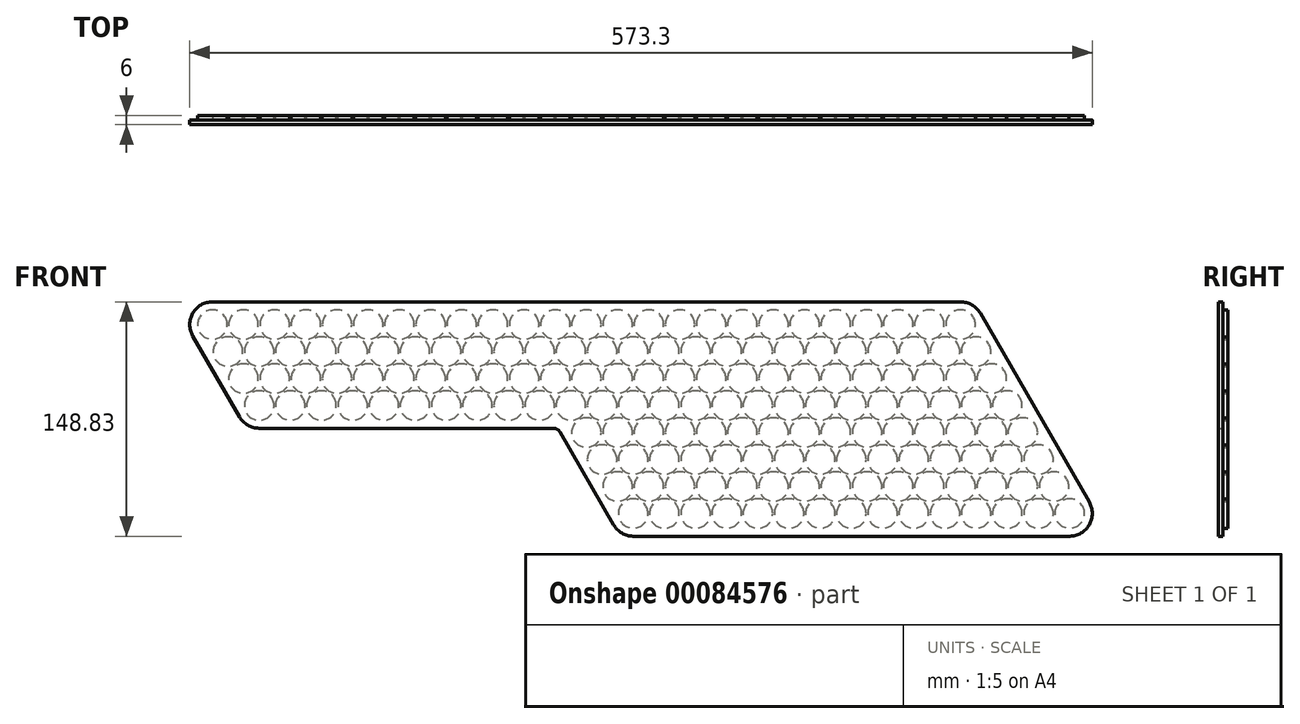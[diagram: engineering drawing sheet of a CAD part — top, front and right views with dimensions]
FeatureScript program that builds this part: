
annotation { "Feature Type Name" : "Feature", "Feature Type Description" : "" }
export const myFeature = defineFeature(function(context is Context, id is Id, definition is map)
    precondition{}
    {
        {
            var Q0;
            Q0=qCreatedBy(makeId("Front.planeOp"),FACE);
            var sketch = newSketch(context, id + "F0", { "sketchPlane" : qUnion([Q0]) });
            skCircle(sketch, "E0", {"center": v(0, 0) * mm, "radius": 9.4 * mm});
            skCircle(sketch, "E1.0.1.0", {"center": v(9.9, -17.15) * mm, "radius": 9.4 * mm});
            skCircle(sketch, "E1.0.2.0", {"center": v(19.8, -34.3) * mm, "radius": 9.4 * mm});
            skCircle(sketch, "E1.0.3.0", {"center": v(29.7, -51.44) * mm, "radius": 9.4 * mm});
            skCircle(sketch, "E1.1.0.0", {"center": v(19.8, 0) * mm, "radius": 9.4 * mm});
            skCircle(sketch, "E1.1.1.0", {"center": v(29.7, -17.15) * mm, "radius": 9.4 * mm});
            skCircle(sketch, "E1.1.2.0", {"center": v(39.6, -34.3) * mm, "radius": 9.4 * mm});
            skCircle(sketch, "E1.1.3.0", {"center": v(49.5, -51.44) * mm, "radius": 9.4 * mm});
            skCircle(sketch, "E1.2.0.0", {"center": v(39.6, 0) * mm, "radius": 9.4 * mm});
            skCircle(sketch, "E1.2.1.0", {"center": v(49.5, -17.15) * mm, "radius": 9.4 * mm});
            skCircle(sketch, "E1.2.2.0", {"center": v(59.4, -34.3) * mm, "radius": 9.4 * mm});
            skCircle(sketch, "E1.2.3.0", {"center": v(69.3, -51.44) * mm, "radius": 9.4 * mm});
            skCircle(sketch, "E1.3.0.0", {"center": v(59.4, 0) * mm, "radius": 9.4 * mm});
            skCircle(sketch, "E1.3.1.0", {"center": v(69.3, -17.15) * mm, "radius": 9.4 * mm});
            skCircle(sketch, "E1.3.2.0", {"center": v(79.2, -34.3) * mm, "radius": 9.4 * mm});
            skCircle(sketch, "E1.3.3.0", {"center": v(89.1, -51.44) * mm, "radius": 9.4 * mm});
            skCircle(sketch, "E1.4.0.0", {"center": v(79.2, 0) * mm, "radius": 9.4 * mm});
            skCircle(sketch, "E1.4.1.0", {"center": v(89.1, -17.15) * mm, "radius": 9.4 * mm});
            skCircle(sketch, "E1.4.2.0", {"center": v(99, -34.3) * mm, "radius": 9.4 * mm});
            skCircle(sketch, "E1.4.3.0", {"center": v(108.9, -51.44) * mm, "radius": 9.4 * mm});
            skCircle(sketch, "E1.5.0.0", {"center": v(99, 0) * mm, "radius": 9.4 * mm});
            skCircle(sketch, "E1.5.1.0", {"center": v(108.9, -17.15) * mm, "radius": 9.4 * mm});
            skCircle(sketch, "E1.5.2.0", {"center": v(118.8, -34.3) * mm, "radius": 9.4 * mm});
            skCircle(sketch, "E1.5.3.0", {"center": v(128.7, -51.44) * mm, "radius": 9.4 * mm});
            skCircle(sketch, "E1.6.0.0", {"center": v(118.8, 0) * mm, "radius": 9.4 * mm});
            skCircle(sketch, "E1.6.1.0", {"center": v(128.7, -17.15) * mm, "radius": 9.4 * mm});
            skCircle(sketch, "E1.6.2.0", {"center": v(138.6, -34.3) * mm, "radius": 9.4 * mm});
            skCircle(sketch, "E1.6.3.0", {"center": v(148.5, -51.44) * mm, "radius": 9.4 * mm});
            skCircle(sketch, "E1.7.0.0", {"center": v(138.6, 0) * mm, "radius": 9.4 * mm});
            skCircle(sketch, "E1.7.1.0", {"center": v(148.5, -17.15) * mm, "radius": 9.4 * mm});
            skCircle(sketch, "E1.7.2.0", {"center": v(158.4, -34.3) * mm, "radius": 9.4 * mm});
            skCircle(sketch, "E1.7.3.0", {"center": v(168.3, -51.44) * mm, "radius": 9.4 * mm});
            skCircle(sketch, "E1.8.0.0", {"center": v(158.4, 0) * mm, "radius": 9.4 * mm});
            skCircle(sketch, "E1.8.1.0", {"center": v(168.3, -17.15) * mm, "radius": 9.4 * mm});
            skCircle(sketch, "E1.8.2.0", {"center": v(178.2, -34.3) * mm, "radius": 9.4 * mm});
            skCircle(sketch, "E1.8.3.0", {"center": v(188.1, -51.44) * mm, "radius": 9.4 * mm});
            skCircle(sketch, "E1.9.0.0", {"center": v(178.2, 0) * mm, "radius": 9.4 * mm});
            skCircle(sketch, "E1.9.1.0", {"center": v(188.1, -17.15) * mm, "radius": 9.4 * mm});
            skCircle(sketch, "E1.9.2.0", {"center": v(198, -34.3) * mm, "radius": 9.4 * mm});
            skCircle(sketch, "E1.9.3.0", {"center": v(207.9, -51.44) * mm, "radius": 9.4 * mm});
            skLineSegment(sketch, "E1.direction1", {"start": v(0, 0) * mm, "end": v(19.8, 0) * mm, "construction": true});
            skLineSegment(sketch, "E1.direction2", {"start": v(0, 0) * mm, "end": v(9.9, -17.15) * mm, "construction": true});
            skCircle(sketch, "E2.0.10.0", {"center": v(198, 0) * mm, "radius": 9.4 * mm});
            skCircle(sketch, "E2.0.10.1", {"center": v(207.9, -17.15) * mm, "radius": 9.4 * mm});
            skCircle(sketch, "E2.0.10.2", {"center": v(217.8, -34.3) * mm, "radius": 9.4 * mm});
            skCircle(sketch, "E2.0.10.3", {"center": v(227.7, -51.44) * mm, "radius": 9.4 * mm});
            skCircle(sketch, "E2.0.11.0", {"center": v(217.8, 0) * mm, "radius": 9.4 * mm});
            skCircle(sketch, "E2.0.11.1", {"center": v(227.7, -17.15) * mm, "radius": 9.4 * mm});
            skCircle(sketch, "E2.0.11.2", {"center": v(237.6, -34.3) * mm, "radius": 9.4 * mm});
            skCircle(sketch, "E2.0.11.3", {"center": v(247.5, -51.44) * mm, "radius": 9.4 * mm});
            skCircle(sketch, "E2.0.12.0", {"center": v(237.6, 0) * mm, "radius": 9.4 * mm});
            skCircle(sketch, "E2.0.12.1", {"center": v(247.5, -17.15) * mm, "radius": 9.4 * mm});
            skCircle(sketch, "E2.0.12.2", {"center": v(257.4, -34.3) * mm, "radius": 9.4 * mm});
            skCircle(sketch, "E2.0.12.3", {"center": v(267.3, -51.44) * mm, "radius": 9.4 * mm});
            skCircle(sketch, "E2.0.13.0", {"center": v(257.4, 0) * mm, "radius": 9.4 * mm});
            skCircle(sketch, "E2.0.13.1", {"center": v(267.3, -17.15) * mm, "radius": 9.4 * mm});
            skCircle(sketch, "E2.0.13.2", {"center": v(277.2, -34.3) * mm, "radius": 9.4 * mm});
            skCircle(sketch, "E2.0.13.3", {"center": v(287.1, -51.44) * mm, "radius": 9.4 * mm});
            skCircle(sketch, "E2.0.14.0", {"center": v(277.2, 0) * mm, "radius": 9.4 * mm});
            skCircle(sketch, "E2.0.14.1", {"center": v(287.1, -17.15) * mm, "radius": 9.4 * mm});
            skCircle(sketch, "E2.0.14.2", {"center": v(297, -34.3) * mm, "radius": 9.4 * mm});
            skCircle(sketch, "E2.0.14.3", {"center": v(306.9, -51.44) * mm, "radius": 9.4 * mm});
            skCircle(sketch, "E2.0.15.0", {"center": v(297, 0) * mm, "radius": 9.4 * mm});
            skCircle(sketch, "E2.0.15.1", {"center": v(306.9, -17.15) * mm, "radius": 9.4 * mm});
            skCircle(sketch, "E2.0.15.2", {"center": v(316.8, -34.3) * mm, "radius": 9.4 * mm});
            skCircle(sketch, "E2.0.15.3", {"center": v(326.7, -51.44) * mm, "radius": 9.4 * mm});
            skCircle(sketch, "E2.0.16.0", {"center": v(316.8, 0) * mm, "radius": 9.4 * mm});
            skCircle(sketch, "E2.0.16.1", {"center": v(326.7, -17.15) * mm, "radius": 9.4 * mm});
            skCircle(sketch, "E2.0.16.2", {"center": v(336.6, -34.3) * mm, "radius": 9.4 * mm});
            skCircle(sketch, "E2.0.16.3", {"center": v(346.5, -51.44) * mm, "radius": 9.4 * mm});
            skCircle(sketch, "E2.0.17.0", {"center": v(336.6, 0) * mm, "radius": 9.4 * mm});
            skCircle(sketch, "E2.0.17.1", {"center": v(346.5, -17.15) * mm, "radius": 9.4 * mm});
            skCircle(sketch, "E2.0.17.2", {"center": v(356.4, -34.3) * mm, "radius": 9.4 * mm});
            skCircle(sketch, "E2.0.17.3", {"center": v(366.3, -51.44) * mm, "radius": 9.4 * mm});
            skCircle(sketch, "E2.0.18.0", {"center": v(356.4, 0) * mm, "radius": 9.4 * mm});
            skCircle(sketch, "E2.0.18.1", {"center": v(366.3, -17.15) * mm, "radius": 9.4 * mm});
            skCircle(sketch, "E2.0.18.2", {"center": v(376.2, -34.3) * mm, "radius": 9.4 * mm});
            skCircle(sketch, "E2.0.18.3", {"center": v(386.1, -51.44) * mm, "radius": 9.4 * mm});
            skCircle(sketch, "E2.0.19.0", {"center": v(376.2, 0) * mm, "radius": 9.4 * mm});
            skCircle(sketch, "E2.0.19.1", {"center": v(386.1, -17.15) * mm, "radius": 9.4 * mm});
            skCircle(sketch, "E2.0.19.2", {"center": v(396, -34.3) * mm, "radius": 9.4 * mm});
            skCircle(sketch, "E2.0.19.3", {"center": v(405.9, -51.44) * mm, "radius": 9.4 * mm});
            skCircle(sketch, "E3.0.20.0", {"center": v(396, 0) * mm, "radius": 9.4 * mm});
            skCircle(sketch, "E3.0.20.1", {"center": v(405.9, -17.15) * mm, "radius": 9.4 * mm});
            skCircle(sketch, "E3.0.20.2", {"center": v(415.8, -34.3) * mm, "radius": 9.4 * mm});
            skCircle(sketch, "E3.0.20.3", {"center": v(425.7, -51.44) * mm, "radius": 9.4 * mm});
            skCircle(sketch, "E3.0.21.0", {"center": v(415.8, 0) * mm, "radius": 9.4 * mm});
            skCircle(sketch, "E3.0.21.1", {"center": v(425.7, -17.15) * mm, "radius": 9.4 * mm});
            skCircle(sketch, "E3.0.21.2", {"center": v(435.6, -34.3) * mm, "radius": 9.4 * mm});
            skCircle(sketch, "E3.0.21.3", {"center": v(445.5, -51.44) * mm, "radius": 9.4 * mm});
            skCircle(sketch, "E3.0.22.0", {"center": v(435.6, 0) * mm, "radius": 9.4 * mm});
            skCircle(sketch, "E3.0.22.1", {"center": v(445.5, -17.15) * mm, "radius": 9.4 * mm});
            skCircle(sketch, "E3.0.22.2", {"center": v(455.4, -34.3) * mm, "radius": 9.4 * mm});
            skCircle(sketch, "E3.0.22.3", {"center": v(465.3, -51.44) * mm, "radius": 9.4 * mm});
            skCircle(sketch, "E3.0.23.0", {"center": v(455.4, 0) * mm, "radius": 9.4 * mm});
            skCircle(sketch, "E3.0.23.1", {"center": v(465.3, -17.15) * mm, "radius": 9.4 * mm});
            skCircle(sketch, "E3.0.23.2", {"center": v(475.2, -34.3) * mm, "radius": 9.4 * mm});
            skCircle(sketch, "E3.0.23.3", {"center": v(485.1, -51.44) * mm, "radius": 9.4 * mm});
            skCircle(sketch, "E3.0.24.0", {"center": v(475.2, 0) * mm, "radius": 9.4 * mm});
            skCircle(sketch, "E3.0.24.1", {"center": v(485.1, -17.15) * mm, "radius": 9.4 * mm});
            skCircle(sketch, "E3.0.24.2", {"center": v(495, -34.3) * mm, "radius": 9.4 * mm});
            skCircle(sketch, "E3.0.24.3", {"center": v(504.9, -51.44) * mm, "radius": 9.4 * mm});
            skLineSegment(sketch, "E4", {"start": v(227.7, -51.44) * mm, "end": v(198, 0) * mm, "construction": true});
            skLineSegment(sketch, "E5", {"start": v(277.2, 0) * mm, "end": v(247.5, -51.44) * mm, "construction": true});
            skLineSegment(sketch, "E6", {"start": v(227.7, -51.44) * mm, "end": v(247.5, -85.74) * mm, "construction": true});
            skLineSegment(sketch, "E7", {"start": v(247.5, -51.44) * mm, "end": v(227.7, -85.74) * mm, "construction": true});
            skCircle(sketch, "E8", {"center": v(237.6, -68.59) * mm, "radius": 9.4 * mm});
            skCircle(sketch, "E9.0.1.0", {"center": v(247.5, -85.74) * mm, "radius": 9.4 * mm});
            skCircle(sketch, "E9.0.2.0", {"center": v(257.4, -102.88) * mm, "radius": 9.4 * mm});
            skCircle(sketch, "E9.0.3.0", {"center": v(267.3, -120.03) * mm, "radius": 9.4 * mm});
            skCircle(sketch, "E9.1.0.0", {"center": v(257.4, -68.59) * mm, "radius": 9.4 * mm});
            skCircle(sketch, "E9.1.1.0", {"center": v(267.3, -85.74) * mm, "radius": 9.4 * mm});
            skCircle(sketch, "E9.1.2.0", {"center": v(277.2, -102.88) * mm, "radius": 9.4 * mm});
            skCircle(sketch, "E9.1.3.0", {"center": v(287.1, -120.03) * mm, "radius": 9.4 * mm});
            skCircle(sketch, "E9.2.0.0", {"center": v(277.2, -68.59) * mm, "radius": 9.4 * mm});
            skCircle(sketch, "E9.2.1.0", {"center": v(287.1, -85.74) * mm, "radius": 9.4 * mm});
            skCircle(sketch, "E9.2.2.0", {"center": v(297, -102.88) * mm, "radius": 9.4 * mm});
            skCircle(sketch, "E9.2.3.0", {"center": v(306.9, -120.03) * mm, "radius": 9.4 * mm});
            skCircle(sketch, "E9.3.0.0", {"center": v(297, -68.59) * mm, "radius": 9.4 * mm});
            skCircle(sketch, "E9.3.1.0", {"center": v(306.9, -85.74) * mm, "radius": 9.4 * mm});
            skCircle(sketch, "E9.3.2.0", {"center": v(316.8, -102.88) * mm, "radius": 9.4 * mm});
            skCircle(sketch, "E9.3.3.0", {"center": v(326.7, -120.03) * mm, "radius": 9.4 * mm});
            skCircle(sketch, "E9.4.0.0", {"center": v(316.8, -68.59) * mm, "radius": 9.4 * mm});
            skCircle(sketch, "E9.4.1.0", {"center": v(326.7, -85.74) * mm, "radius": 9.4 * mm});
            skCircle(sketch, "E9.4.2.0", {"center": v(336.6, -102.88) * mm, "radius": 9.4 * mm});
            skCircle(sketch, "E9.4.3.0", {"center": v(346.5, -120.03) * mm, "radius": 9.4 * mm});
            skCircle(sketch, "E9.5.0.0", {"center": v(336.6, -68.59) * mm, "radius": 9.4 * mm});
            skCircle(sketch, "E9.5.1.0", {"center": v(346.5, -85.74) * mm, "radius": 9.4 * mm});
            skCircle(sketch, "E9.5.2.0", {"center": v(356.4, -102.88) * mm, "radius": 9.4 * mm});
            skCircle(sketch, "E9.5.3.0", {"center": v(366.3, -120.03) * mm, "radius": 9.4 * mm});
            skCircle(sketch, "E9.6.0.0", {"center": v(356.4, -68.59) * mm, "radius": 9.4 * mm});
            skCircle(sketch, "E9.6.1.0", {"center": v(366.3, -85.74) * mm, "radius": 9.4 * mm});
            skCircle(sketch, "E9.6.2.0", {"center": v(376.2, -102.88) * mm, "radius": 9.4 * mm});
            skCircle(sketch, "E9.6.3.0", {"center": v(386.1, -120.03) * mm, "radius": 9.4 * mm});
            skCircle(sketch, "E9.7.0.0", {"center": v(376.2, -68.59) * mm, "radius": 9.4 * mm});
            skCircle(sketch, "E9.7.1.0", {"center": v(386.1, -85.74) * mm, "radius": 9.4 * mm});
            skCircle(sketch, "E9.7.2.0", {"center": v(396, -102.88) * mm, "radius": 9.4 * mm});
            skCircle(sketch, "E9.7.3.0", {"center": v(405.9, -120.03) * mm, "radius": 9.4 * mm});
            skCircle(sketch, "E9.8.0.0", {"center": v(396, -68.59) * mm, "radius": 9.4 * mm});
            skCircle(sketch, "E9.8.1.0", {"center": v(405.9, -85.74) * mm, "radius": 9.4 * mm});
            skCircle(sketch, "E9.8.2.0", {"center": v(415.8, -102.88) * mm, "radius": 9.4 * mm});
            skCircle(sketch, "E9.8.3.0", {"center": v(425.7, -120.03) * mm, "radius": 9.4 * mm});
            skCircle(sketch, "E9.9.0.0", {"center": v(415.8, -68.59) * mm, "radius": 9.4 * mm});
            skCircle(sketch, "E9.9.1.0", {"center": v(425.7, -85.74) * mm, "radius": 9.4 * mm});
            skCircle(sketch, "E9.9.2.0", {"center": v(435.6, -102.88) * mm, "radius": 9.4 * mm});
            skCircle(sketch, "E9.9.3.0", {"center": v(445.5, -120.03) * mm, "radius": 9.4 * mm});
            skCircle(sketch, "E9.10.0.0", {"center": v(435.6, -68.59) * mm, "radius": 9.4 * mm});
            skCircle(sketch, "E9.10.1.0", {"center": v(445.5, -85.74) * mm, "radius": 9.4 * mm});
            skCircle(sketch, "E9.10.2.0", {"center": v(455.4, -102.88) * mm, "radius": 9.4 * mm});
            skCircle(sketch, "E9.10.3.0", {"center": v(465.3, -120.03) * mm, "radius": 9.4 * mm});
            skCircle(sketch, "E9.11.0.0", {"center": v(455.4, -68.59) * mm, "radius": 9.4 * mm});
            skCircle(sketch, "E9.11.1.0", {"center": v(465.3, -85.74) * mm, "radius": 9.4 * mm});
            skCircle(sketch, "E9.11.2.0", {"center": v(475.2, -102.88) * mm, "radius": 9.4 * mm});
            skCircle(sketch, "E9.11.3.0", {"center": v(485.1, -120.03) * mm, "radius": 9.4 * mm});
            skCircle(sketch, "E9.12.0.0", {"center": v(475.2, -68.59) * mm, "radius": 9.4 * mm});
            skCircle(sketch, "E9.12.1.0", {"center": v(485.1, -85.74) * mm, "radius": 9.4 * mm});
            skCircle(sketch, "E9.12.2.0", {"center": v(495, -102.88) * mm, "radius": 9.4 * mm});
            skCircle(sketch, "E9.12.3.0", {"center": v(504.9, -120.03) * mm, "radius": 9.4 * mm});
            skCircle(sketch, "E9.13.0.0", {"center": v(495, -68.59) * mm, "radius": 9.4 * mm});
            skCircle(sketch, "E9.13.1.0", {"center": v(504.9, -85.74) * mm, "radius": 9.4 * mm});
            skCircle(sketch, "E9.13.2.0", {"center": v(514.8, -102.88) * mm, "radius": 9.4 * mm});
            skCircle(sketch, "E9.13.3.0", {"center": v(524.7, -120.03) * mm, "radius": 9.4 * mm});
            skLineSegment(sketch, "E9.direction1", {"start": v(237.6, -68.59) * mm, "end": v(257.4, -68.59) * mm, "construction": true});
            skLineSegment(sketch, "E9.direction2", {"start": v(237.6, -68.59) * mm, "end": v(247.5, -85.74) * mm, "construction": true});
            skCircle(sketch, "E10.0.14.0", {"center": v(514.8, -68.59) * mm, "radius": 9.4 * mm});
            skCircle(sketch, "E10.0.14.1", {"center": v(524.7, -85.74) * mm, "radius": 9.4 * mm});
            skCircle(sketch, "E10.0.14.2", {"center": v(534.6, -102.88) * mm, "radius": 9.4 * mm});
            skCircle(sketch, "E10.0.14.3", {"center": v(544.5, -120.03) * mm, "radius": 9.4 * mm});
            skSolve(sketch);
        }
        {
            var Q0;
            Q0=qSketchRegion(id+"F0",true);
            extrude(context, id + "F1", {"entities" : qUnion([Q0]), "depth" : 3 * mm});
        }
        {
            var Q0;
            Q0=makeQuery(id+"F1.opExtrude","CAP_FACE",FACE,{"disambiguationData":[OSD([sQuery(id+"F0.wireOp",EDGE,"E0")])],"isStart":false});
            var sketch = newSketch(context, id + "F2", { "sketchPlane" : qUnion([Q0]) });
            skCircle(sketch, "E11.0", {"center": v(0, 0) * mm, "radius": 9.4 * mm});
            skCircle(sketch, "E11.1", {"center": v(29.7, -51.44) * mm, "radius": 9.4 * mm});
            skCircle(sketch, "E11.2", {"center": v(475.2, 0) * mm, "radius": 9.4 * mm});
            skCircle(sketch, "E11.3", {"center": v(544.5, -120.03) * mm, "radius": 9.4 * mm});
            skCircle(sketch, "E11.4", {"center": v(267.3, -120.03) * mm, "radius": 9.4 * mm});
            skCircle(sketch, "E11.5", {"center": v(237.6, -68.59) * mm, "radius": 9.4 * mm});
            skCircle(sketch, "E11.6", {"center": v(227.7, -51.44) * mm, "radius": 9.4 * mm});
            skCircle(sketch, "E12.0", {"center": v(0, 0) * mm, "radius": 14.4 * mm});
            skCircle(sketch, "E13.0", {"center": v(475.2, 0) * mm, "radius": 14.4 * mm});
            skCircle(sketch, "E14.0", {"center": v(544.5, -120.03) * mm, "radius": 14.4 * mm});
            skCircle(sketch, "E15.0", {"center": v(267.3, -120.03) * mm, "radius": 14.4 * mm});
            skCircle(sketch, "E16.0", {"center": v(29.7, -51.44) * mm, "radius": 14.4 * mm});
            skLineSegment(sketch, "E17", {"start": v(0, 14.4) * mm, "end": v(475.2, 14.4) * mm});
            skLineSegment(sketch, "E18", {"start": v(487.67, 7.2) * mm, "end": v(556.97, -112.83) * mm});
            skLineSegment(sketch, "E19", {"start": v(544.5, -134.43) * mm, "end": v(267.3, -134.43) * mm});
            skLineSegment(sketch, "E20", {"start": v(-12.47, -7.2) * mm, "end": v(17.23, -58.64) * mm});
            skLineSegment(sketch, "E21", {"start": v(29.7, -65.84) * mm, "end": v(219.39, -65.84) * mm});
            skLineSegment(sketch, "E22", {"start": v(219.39, -65.84) * mm, "end": v(254.83, -127.23) * mm});
            skSolve(sketch);
        }
        {
            var Q0;
            Q0=qSketchRegion(id+"F2",true);
            var Q1;
            Q1=makeQuery(id+"F2.imprint","IMPRINT",FACE,{"disambiguationData":[TD([[makeQuery(id+"F2.imprint","IMPRINT",EDGE,{"derivedFrom":sQuery(id+"F2.wireOp",EDGE,"E11.2")}),1.0]])]});
            var Q2;
            Q2=makeQuery(id+"F2.imprint","IMPRINT",FACE,{"disambiguationData":[TD([[makeQuery(id+"F2.imprint","IMPRINT",EDGE,{"derivedFrom":sQuery(id+"F2.wireOp",EDGE,"E11.0")}),1.0]])]});
            var Q3;
            Q3=makeQuery(id+"F2.imprint","IMPRINT",FACE,{"disambiguationData":[TD([[makeQuery(id+"F2.imprint","IMPRINT",EDGE,{"derivedFrom":sQuery(id+"F2.wireOp",EDGE,"E11.1")}),1.0]])]});
            var Q4;
            Q4=makeQuery(id+"F2.imprint","IMPRINT",FACE,{"disambiguationData":[TD([[makeQuery(id+"F2.imprint","IMPRINT",EDGE,{"derivedFrom":sQuery(id+"F2.wireOp",EDGE,"E11.6")}),1.0]])]});
            var Q5;
            Q5=makeQuery(id+"F2.imprint","IMPRINT",FACE,{"disambiguationData":[TD([[makeQuery(id+"F2.imprint","IMPRINT",EDGE,{"derivedFrom":sQuery(id+"F2.wireOp",EDGE,"E11.5")}),1.0]])]});
            var Q6;
            Q6=makeQuery(id+"F2.imprint","IMPRINT",FACE,{"disambiguationData":[TD([[makeQuery(id+"F2.imprint","IMPRINT",EDGE,{"derivedFrom":sQuery(id+"F2.wireOp",EDGE,"E11.4")}),1.0]])]});
            var Q7;
            Q7=makeQuery(id+"F2.imprint","IMPRINT",FACE,{"disambiguationData":[TD([[makeQuery(id+"F2.imprint","IMPRINT",EDGE,{"derivedFrom":sQuery(id+"F2.wireOp",EDGE,"E11.3")}),1.0]])]});
            extrude(context, id + "F3", {"entities" : qUnion([Q0, Q1, Q2, Q3, Q4, Q5, Q6, Q7]), "depth" : 3 * mm});
        }
        {
            var Q0;
            Q0=makeQuery(id+"F3.opExtrude","SWEPT_EDGE",EDGE,{"disambiguationData":[OSD([sQuery(id+"F2.wireOp",EDGE,"E21"),sQuery(id+"F2.wireOp",EDGE,"E22")])]});
            fillet(context, id + "F4", {"entities" : qUnion([Q0]), "radius" : 5 * mm, "tangentPropagation" : true, "conicFillet" : false});
        }
    });
